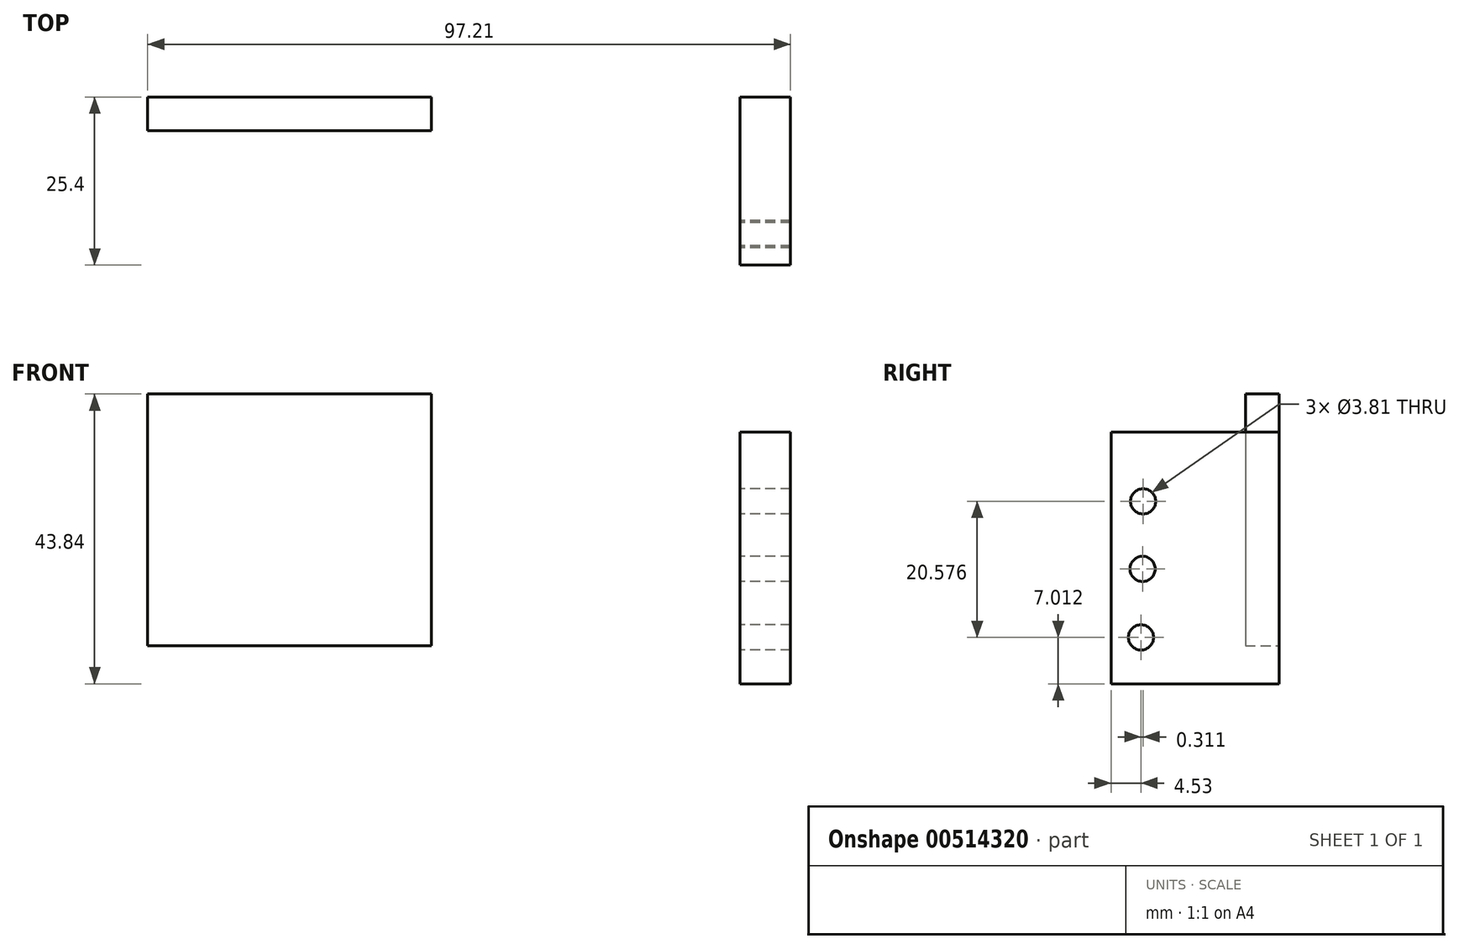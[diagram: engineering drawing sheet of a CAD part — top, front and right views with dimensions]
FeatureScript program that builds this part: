
annotation { "Feature Type Name" : "Feature", "Feature Type Description" : "" }
export const myFeature = defineFeature(function(context is Context, id is Id, definition is map)
    precondition{}
    {
        {
            var Q0;
            Q0=qCreatedBy(makeId("Front.planeOp"),FACE);
            var sketch = newSketch(context, id + "F0", { "sketchPlane" : qUnion([Q0])});
            skLineSegment(sketch, "E0.bottom", {"start": v(-59.08, 81.65) * mm, "end": v(-16.15, 81.65) * mm});
            skLineSegment(sketch, "E0.top", {"start": v(-59.08, 43.55) * mm, "end": v(-16.15, 43.55) * mm});
            skLineSegment(sketch, "E0.left", {"start": v(-59.08, 81.65) * mm, "end": v(-59.08, 43.55) * mm});
            skLineSegment(sketch, "E0.right", {"start": v(-16.15, 81.65) * mm, "end": v(-16.15, 43.55) * mm});
            skSolve(sketch);
        }
        {
            var Q0;
            Q0 = qSketchRegion(id + "F0", true);
            extrude(context, id + "F1", {"entities" : qUnion([Q0]), "depth" : 5.08 * mm});
        }
        {
            var Q0;
            Q0=qCreatedBy(makeId("Front.planeOp"),FACE);
            var sketch = newSketch(context, id + "F2", { "sketchPlane" : qUnion([Q0])});
            skLineSegment(sketch, "E1.bottom", {"start": v(30.51, 75.9) * mm, "end": v(38.13, 75.9) * mm});
            skLineSegment(sketch, "E1.top", {"start": v(30.51, 37.8) * mm, "end": v(38.13, 37.8) * mm});
            skLineSegment(sketch, "E1.left", {"start": v(30.51, 75.9) * mm, "end": v(30.51, 37.8) * mm});
            skLineSegment(sketch, "E1.right", {"start": v(38.13, 75.9) * mm, "end": v(38.13, 37.8) * mm});
            skSolve(sketch);
        }
        {
            var Q0;
            Q0 = qSketchRegion(id + "F2", true);
            extrude(context, id + "F3", {"entities" : qUnion([Q0]), "depth" : 25.4 * mm});
        }
        {
            var Q0;
            Q0=makeQuery(id+"F3.opExtrude","SWEPT_FACE",FACE,{"disambiguationData":[OSD([sQuery(id+"F2.wireOp",EDGE,"E1.left")])]});
            var sketch = newSketch(context, id + "F4", { "sketchPlane" : qUnion([Q0])});
            skCircle(sketch, "E2", {"center": v(20.56, 65.4) * mm, "radius": 1.9 * mm});
            skCircle(sketch, "E3", {"center": v(20.64, 55.19) * mm, "radius": 1.9 * mm});
            skCircle(sketch, "E4", {"center": v(20.87, 44.82) * mm, "radius": 1.9 * mm});
            skSolve(sketch);
        }
        {
            var Q0;
            Q0 = qSketchRegion(id + "F4", true);
            extrude(context, id + "F5", {"entities" : qUnion([Q0]), "operationType" : NewBodyOperationType.REMOVE, "oppositeDirection" : true, "depth" : 25.4 * mm});
        }
    });
